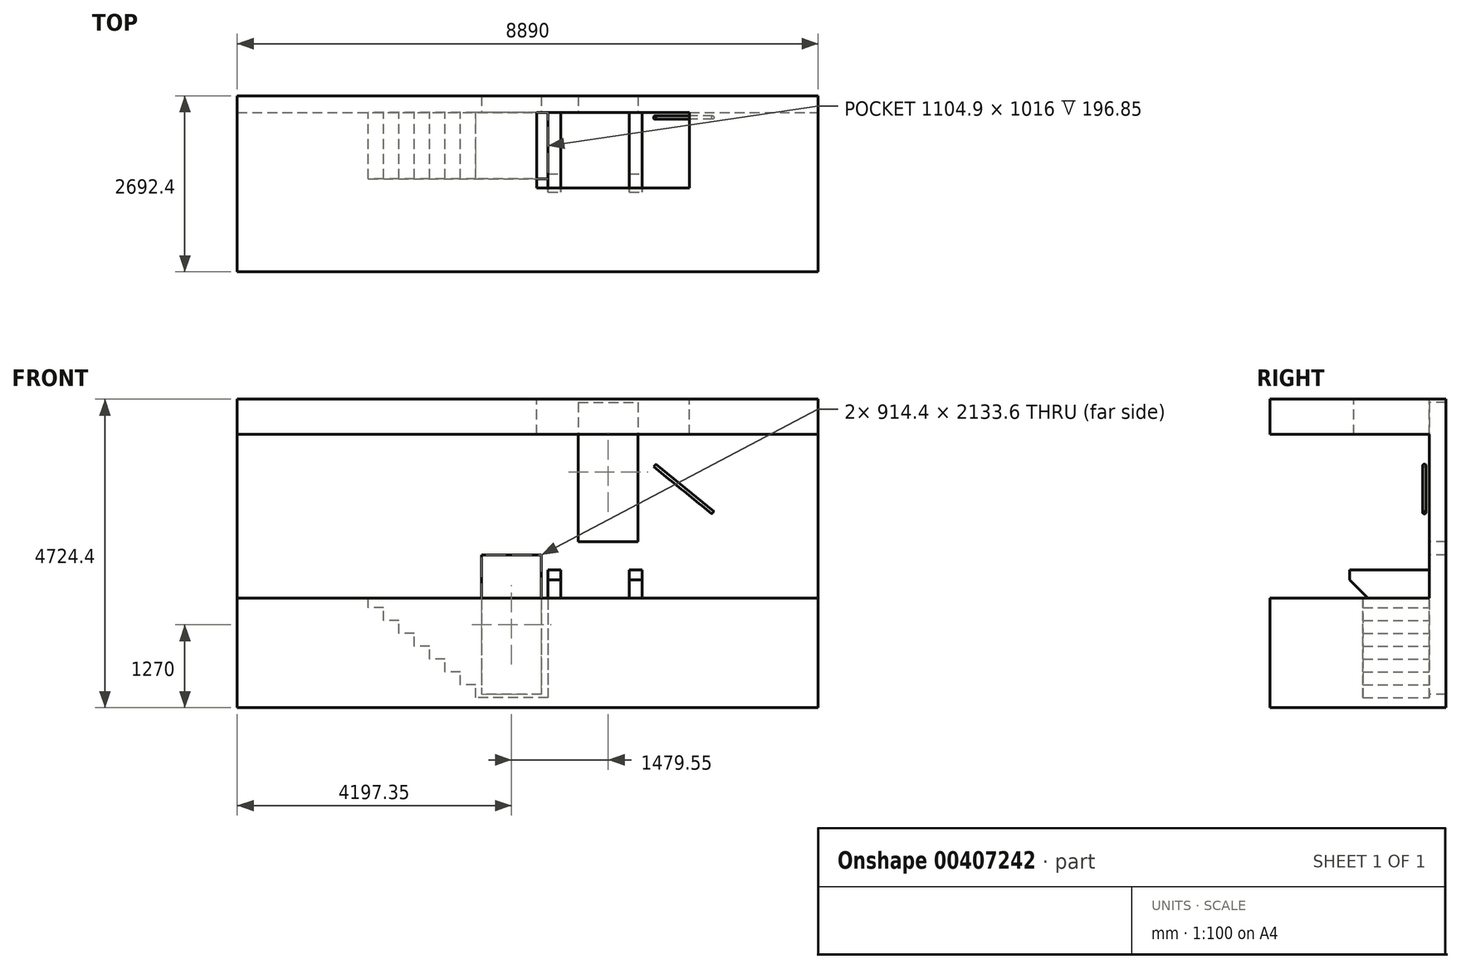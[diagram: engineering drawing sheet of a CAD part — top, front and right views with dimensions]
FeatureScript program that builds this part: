
annotation { "Feature Type Name" : "Feature", "Feature Type Description" : "" }
export const myFeature = defineFeature(function(context is Context, id is Id, definition is map)
    precondition{}
    {
        {
            var Q0;
            Q0=qCreatedBy(makeId("Top.planeOp"),FACE);
            var sketch = newSketch(context, id + "F0", { "sketchPlane" : qUnion([Q0])});
            skLineSegment(sketch, "E0.bottom", {"start": v(-6134.1, 0) * mm, "end": v(2755.9, 0) * mm});
            skLineSegment(sketch, "E0.top", {"start": v(-6134.1, -2438.4) * mm, "end": v(2755.9, -2438.4) * mm});
            skLineSegment(sketch, "E0.left", {"start": v(-6134.1, 0) * mm, "end": v(-6134.1, -2438.4) * mm});
            skLineSegment(sketch, "E0.right", {"start": v(2755.9, 0) * mm, "end": v(2755.9, -2438.4) * mm});
            skSolve(sketch);
        }
        {
            var Q0;
            Q0 = qSketchRegion(id + "F0", true);
            extrude(context, id + "F1", {"entities" : qUnion([Q0]), "oppositeDirection" : true, "depth" : 1676.4 * mm});
        }
        {
            var Q0;
            Q0=makeQuery(id+"F1.opExtrude","SWEPT_FACE",FACE,{"disambiguationData":[OSD([sQuery(id+"F0.wireOp",EDGE,"E0.bottom")])]});
            var sketch = newSketch(context, id + "F2", { "sketchPlane" : qUnion([Q0])});
            skLineSegment(sketch, "E1.top", {"start": v(6134.1, 3048) * mm, "end": v(-2755.9, 3048) * mm});
            skLineSegment(sketch, "E1.left", {"start": v(6134.1, 0) * mm, "end": v(6134.1, 3048) * mm});
            skLineSegment(sketch, "E1.right", {"start": v(-2755.9, 0) * mm, "end": v(-2755.9, 3048) * mm});
            skLineSegment(sketch, "E2.bottom", {"start": v(914.4, 2997.2) * mm, "end": v(0, 2997.2) * mm});
            skLineSegment(sketch, "E2.top", {"start": v(914.4, 863.6) * mm, "end": v(0, 863.6) * mm});
            skLineSegment(sketch, "E2.left", {"start": v(914.4, 2997.2) * mm, "end": v(914.4, 863.6) * mm});
            skLineSegment(sketch, "E2.right", {"start": v(0, 2997.2) * mm, "end": v(0, 863.6) * mm});
            skLineSegment(sketch, "E3.0", {"start": v(6134.1, -1676.4) * mm, "end": v(-2755.9, -1676.4) * mm});
            skLineSegment(sketch, "E4.0", {"start": v(6134.1, -1676.4) * mm, "end": v(6134.1, 0) * mm});
            skLineSegment(sketch, "E5.0", {"start": v(-2755.9, -1676.4) * mm, "end": v(-2755.9, 0) * mm});
            skSolve(sketch);
        }
        {
            var Q0;
            Q0 = qSketchRegion(id + "F2", true);
            extrude(context, id + "F3", {"entities" : qUnion([Q0]), "operationType" : NewBodyOperationType.ADD, "depth" : 254 * mm});
        }
        {
            var Q0;
            Q0=makeQuery(id+"F3.boolean.opBoolean","MERGE",FACE,{"derivedFrom":[makeQuery(id+"F1.opExtrude","SWEPT_FACE",FACE,{"disambiguationData":[OSD([sQuery(id+"F0.wireOp",EDGE,"E0.right")])]}),makeQuery(id+"F3.opExtrude","SWEPT_FACE",FACE,{"disambiguationData":[OSD([sQuery(id+"F2.wireOp",EDGE,"E1.right"),sQuery(id+"F2.wireOp",EDGE,"E5.0")])]})]});
            cPlane(context, id + "F4", {"entities" : qUnion([Q0]), "cplaneType" : CPlaneType.OFFSET, "offset" : 2692.4 * mm, "oppositeDirection" : true, "width" : 152.4 * mm, "height" : 152.4 * mm});
        }
        {
            var Q0;
            Q0=qCreatedBy(id+"F4.planeOp",FACE);
            cPlane(context, id + "F5", {"entities" : qUnion([Q0]), "cplaneType" : CPlaneType.OFFSET, "offset" : 1441.45 * mm, "oppositeDirection" : true, "width" : 152.4 * mm, "height" : 152.4 * mm});
        }
        {
            var Q0;
            Q0=qCreatedBy(id+"F4.planeOp",FACE);
            var sketch = newSketch(context, id + "F6", { "sketchPlane" : qUnion([Q0])});
            skLineSegment(sketch, "E6.0", {"start": v(0, 0) * mm, "end": v(-939.8, 0) * mm});
            skLineSegment(sketch, "E7.0", {"start": v(0, 0) * mm, "end": v(0, 431.8) * mm});
            skLineSegment(sketch, "E8", {"start": v(0, 431.8) * mm, "end": v(-1219.2, 431.8) * mm});
            skLineSegment(sketch, "E9", {"start": v(-1219.2, 431.8) * mm, "end": v(-1219.2, 279.4) * mm});
            skLineSegment(sketch, "E10", {"start": v(-1219.2, 279.4) * mm, "end": v(-939.8, 0) * mm});
            skPoint(sketch, "E11.orphan", {"position": v(-2438.4, 0) * mm});
            skPoint(sketch, "E12.orphan", {"position": v(0, 3048) * mm});
            skSolve(sketch);
        }
        {
            var Q0;
            Q0=makeQuery(id+"F6.imprint","IMPRINT",FACE,{"disambiguationData":[TD([[makeQuery(id+"F6.imprint","IMPRINT",EDGE,{"derivedFrom":sQuery(id+"F6.wireOp",EDGE,"E6.0")}),-1.0]])]});
            var Q1;
            Q1=qCreatedBy(id+"F5.planeOp",FACE);
            extrude(context, id + "F7", {"entities" : qUnion([Q0]), "operationType" : NewBodyOperationType.ADD, "endBound" : BoundingType.UP_TO_SURFACE, "oppositeDirection" : true, "endBoundEntityFace" : qUnion([Q1]), "depth" : 196.85 * mm});
        }
        {
            var Q0;
            Q0=makeQuery(id+"F7.opExtrude","SWEPT_FACE",FACE,{"disambiguationData":[OSD([sQuery(id+"F6.wireOp",EDGE,"E8")])]});
            var sketch = newSketch(context, id + "F8", { "sketchPlane" : qUnion([Q0])});
            skLineSegment(sketch, "E13.bottom", {"start": v(-1181.1, 0) * mm, "end": v(-133.35, 0) * mm});
            skLineSegment(sketch, "E13.top", {"start": v(-1181.1, -1219.2) * mm, "end": v(-133.35, -1219.2) * mm});
            skLineSegment(sketch, "E13.left", {"start": v(-1181.1, 0) * mm, "end": v(-1181.1, -1219.2) * mm});
            skLineSegment(sketch, "E13.right", {"start": v(-133.35, 0) * mm, "end": v(-133.35, -1219.2) * mm});
            skSolve(sketch);
        }
        {
            var Q0;
            Q0=makeQuery(id+"F8.imprint","IMPRINT",FACE,{"disambiguationData":[TD([[makeQuery(id+"F8.imprint","IMPRINT",EDGE,{"derivedFrom":sQuery(id+"F8.wireOp",EDGE,"E13.bottom")}),-1.0]])]});
            var Q1;
            Q1=makeQuery(id+"F1.opExtrude","CAP_FACE",FACE,{"disambiguationData":[OSD([sQuery(id+"F0.wireOp",EDGE,"E0.bottom"),sQuery(id+"F0.wireOp",EDGE,"E0.top"),sQuery(id+"F0.wireOp",EDGE,"E0.left"),sQuery(id+"F0.wireOp",EDGE,"E0.right")])],"isStart":true});
            extrude(context, id + "F9", {"entities" : qUnion([Q0]), "operationType" : NewBodyOperationType.REMOVE, "endBound" : BoundingType.UP_TO_SURFACE, "oppositeDirection" : true, "endBoundEntityFace" : qUnion([Q1]), "depth" : 25.4 * mm});
        }
        {
            var Q0;
            Q0=makeQuery(id+"F9.boolean.opBoolean","MERGE",FACE,{"derivedFrom":[makeQuery(id+"F3.opExtrude","CAP_FACE",FACE,{"disambiguationData":[OSD([sQuery(id+"F2.wireOp",EDGE,"E1.top"),sQuery(id+"F2.wireOp",EDGE,"E1.left"),sQuery(id+"F2.wireOp",EDGE,"E1.right"),sQuery(id+"F2.wireOp",EDGE,"E2.bottom"),sQuery(id+"F2.wireOp",EDGE,"E2.top"),sQuery(id+"F2.wireOp",EDGE,"E2.left"),sQuery(id+"F2.wireOp",EDGE,"E2.right"),sQuery(id+"F2.wireOp",EDGE,"E3.0"),sQuery(id+"F2.wireOp",EDGE,"E4.0"),sQuery(id+"F2.wireOp",EDGE,"E5.0")])],"isStart":true}),makeQuery(id+"F9.opExtrude","SWEPT_FACE",FACE,{"disambiguationData":[OSD([sQuery(id+"F8.wireOp",EDGE,"E13.bottom")])]})]});
            var sketch = newSketch(context, id + "F10", { "sketchPlane" : qUnion([Q0])});
            skLineSegment(sketch, "E14", {"start": v(-1377.95, 0) * mm, "end": v(-1377.95, -1524) * mm});
            skLineSegment(sketch, "E15", {"start": v(-1377.95, -1524) * mm, "end": v(-2482.85, -1524) * mm});
            skLineSegment(sketch, "E16", {"start": v(-2482.85, -1524) * mm, "end": v(-2482.85, -1327.15) * mm});
            skLineSegment(sketch, "E17", {"start": v(-2482.85, -1327.15) * mm, "end": v(-2717.8, -1327.15) * mm});
            skLineSegment(sketch, "E18", {"start": v(-2717.8, -1327.15) * mm, "end": v(-2717.8, -1130.3) * mm});
            skLineSegment(sketch, "E19", {"start": v(-2717.8, -1130.3) * mm, "end": v(-2952.75, -1130.3) * mm});
            skLineSegment(sketch, "E20", {"start": v(-2952.75, -1130.3) * mm, "end": v(-2952.75, -933.45) * mm});
            skLineSegment(sketch, "E21", {"start": v(-2952.75, -933.45) * mm, "end": v(-3187.7, -933.45) * mm});
            skLineSegment(sketch, "E22", {"start": v(-3187.7, -933.45) * mm, "end": v(-3187.7, -736.6) * mm});
            skLineSegment(sketch, "E23", {"start": v(-3187.7, -736.6) * mm, "end": v(-3422.65, -736.6) * mm});
            skLineSegment(sketch, "E24", {"start": v(-3422.65, -736.6) * mm, "end": v(-3422.65, -539.75) * mm});
            skLineSegment(sketch, "E25", {"start": v(-3422.65, -539.75) * mm, "end": v(-3657.6, -539.75) * mm});
            skLineSegment(sketch, "E26", {"start": v(-3657.6, -539.75) * mm, "end": v(-3657.6, -342.9) * mm});
            skLineSegment(sketch, "E27", {"start": v(-3657.6, -342.9) * mm, "end": v(-3892.55, -342.9) * mm});
            skLineSegment(sketch, "E28", {"start": v(-3892.55, -342.9) * mm, "end": v(-3892.55, -146.05) * mm});
            skLineSegment(sketch, "E29", {"start": v(-1377.95, 0) * mm, "end": v(-4127.5, 0) * mm});
            skLineSegment(sketch, "E30", {"start": v(-3892.55, -146.05) * mm, "end": v(-4127.5, -146.05) * mm});
            skLineSegment(sketch, "E31", {"start": v(-4127.5, -146.05) * mm, "end": v(-4127.5, 0) * mm});
            skSolve(sketch);
        }
        {
            var Q0;
            Q0 = qSketchRegion(id + "F10", true);
            extrude(context, id + "F11", {"entities" : qUnion([Q0]), "operationType" : NewBodyOperationType.REMOVE, "depth" : 1016 * mm});
        }
        {
            var Q0;
            Q0=makeQuery(id+"F3.opExtrude","SWEPT_FACE",FACE,{"disambiguationData":[OSD([sQuery(id+"F2.wireOp",EDGE,"E1.top")])]});
            var sketch = newSketch(context, id + "F12", { "sketchPlane" : qUnion([Q0])});
            skLineSegment(sketch, "E32.0", {"start": v(-6134.1, 0) * mm, "end": v(-6134.1, -2438.4) * mm});
            skLineSegment(sketch, "E33.0", {"start": v(-6134.1, -2438.4) * mm, "end": v(2755.9, -2438.4) * mm});
            skLineSegment(sketch, "E34.0", {"start": v(2755.9, 0) * mm, "end": v(2755.9, -2438.4) * mm});
            skLineSegment(sketch, "E35.0", {"start": v(-6134.1, 0) * mm, "end": v(-1549.4, 0) * mm});
            skLineSegment(sketch, "E36", {"start": v(-1549.4, 0) * mm, "end": v(-1549.4, -1155.7) * mm});
            skLineSegment(sketch, "E37", {"start": v(-1549.4, -1155.7) * mm, "end": v(787.4, -1155.7) * mm});
            skLineSegment(sketch, "E38", {"start": v(787.4, -1155.7) * mm, "end": v(787.4, 0) * mm});
            skLineSegment(sketch, "E39.trimOffspring", {"start": v(787.4, 0) * mm, "end": v(2755.9, 0) * mm});
            skSolve(sketch);
        }
        {
            var Q0;
            Q0 = qSketchRegion(id + "F12", true);
            extrude(context, id + "F13", {"entities" : qUnion([Q0]), "operationType" : NewBodyOperationType.ADD, "oppositeDirection" : true, "depth" : 539.75 * mm});
        }
        {
            var Q0;
            Q0=makeQuery(id+"F11.boolean.opBoolean","MERGE",FACE,{"derivedFrom":[makeQuery(id+"F9.boolean.opBoolean","MERGE",FACE,{"derivedFrom":[makeQuery(id+"F3.opExtrude","CAP_FACE",FACE,{"disambiguationData":[OSD([sQuery(id+"F2.wireOp",EDGE,"E1.top"),sQuery(id+"F2.wireOp",EDGE,"E1.left"),sQuery(id+"F2.wireOp",EDGE,"E1.right"),sQuery(id+"F2.wireOp",EDGE,"E2.bottom"),sQuery(id+"F2.wireOp",EDGE,"E2.top"),sQuery(id+"F2.wireOp",EDGE,"E2.left"),sQuery(id+"F2.wireOp",EDGE,"E2.right"),sQuery(id+"F2.wireOp",EDGE,"E3.0"),sQuery(id+"F2.wireOp",EDGE,"E4.0"),sQuery(id+"F2.wireOp",EDGE,"E5.0")])],"isStart":true}),makeQuery(id+"F9.opExtrude","SWEPT_FACE",FACE,{"disambiguationData":[OSD([sQuery(id+"F8.wireOp",EDGE,"E13.bottom")])]})]}),makeQuery(id+"F11.opExtrude","CAP_FACE",FACE,{"disambiguationData":[OSD([sQuery(id+"F10.wireOp",EDGE,"E14"),sQuery(id+"F10.wireOp",EDGE,"E15"),sQuery(id+"F10.wireOp",EDGE,"E16"),sQuery(id+"F10.wireOp",EDGE,"E17"),sQuery(id+"F10.wireOp",EDGE,"E18"),sQuery(id+"F10.wireOp",EDGE,"E19"),sQuery(id+"F10.wireOp",EDGE,"E20"),sQuery(id+"F10.wireOp",EDGE,"E21"),sQuery(id+"F10.wireOp",EDGE,"E22"),sQuery(id+"F10.wireOp",EDGE,"E23"),sQuery(id+"F10.wireOp",EDGE,"E24"),sQuery(id+"F10.wireOp",EDGE,"E25"),sQuery(id+"F10.wireOp",EDGE,"E26"),sQuery(id+"F10.wireOp",EDGE,"E27"),sQuery(id+"F10.wireOp",EDGE,"E28"),sQuery(id+"F10.wireOp",EDGE,"E29"),sQuery(id+"F10.wireOp",EDGE,"E30"),sQuery(id+"F10.wireOp",EDGE,"E31")])],"isStart":true})]});
            cPlane(context, id + "F14", {"entities" : qUnion([Q0]), "cplaneType" : CPlaneType.OFFSET, "offset" : 76.2 * mm, "width" : 152.4 * mm, "height" : 152.4 * mm});
        }
        {
            var Q0;
            Q0=qCreatedBy(id+"F14.planeOp",FACE);
            var sketch = newSketch(context, id + "F15", { "sketchPlane" : qUnion([Q0])});
            skLineSegment(sketch, "E40", {"start": v(254, 2032) * mm, "end": v(1143, 1311.33) * mm});
            skPoint(sketch, "E41", {"position": v(1143, 1311.33) * mm});
            skPoint(sketch, "E42", {"position": v(254, 2032) * mm});
            skSolve(sketch);
        }
        {
            var Q0;
            Q0=sQuery(id+"F15.wireOp",VERTEX,"E41");
            var Q1;
            Q1=sQuery(id+"F15.wireOp",EDGE,"E40");
            cPlane(context, id + "F16", {"entities" : qUnion([Q0, Q1]), "cplaneType" : CPlaneType.LINE_POINT, "offset" : 25.4 * mm, "width" : 152.4 * mm, "height" : 152.4 * mm});
        }
        {
            var Q0;
            Q0=qCreatedBy(id+"F16.planeOp",FACE);
            var sketch = newSketch(context, id + "F17", { "sketchPlane" : qUnion([Q0])});
            skCircle(sketch, "E43", {"center": v(-76.2, 1738.44) * mm, "radius": 25.4 * mm});
            skSolve(sketch);
        }
        {
            var Q0;
            Q0=makeQuery(id+"F17.imprint","IMPRINT",FACE,{"disambiguationData":[TD([[makeQuery(id+"F17.imprint","IMPRINT",EDGE,{"derivedFrom":sQuery(id+"F17.wireOp",EDGE,"E43")}),1.0]])]});
            var Q1;
            Q1=sQuery(id+"F15.wireOp",EDGE,"E40");
            sweep(context, id + "F18", {"profiles" : qUnion([Q0]), "path" : qUnion([Q1])});
        }
        {
            var Q0;
            Q0=makeQuery(id+"F11.boolean.opBoolean","MERGE",FACE,{"derivedFrom":[makeQuery(id+"F9.boolean.opBoolean","MERGE",FACE,{"derivedFrom":[makeQuery(id+"F3.opExtrude","CAP_FACE",FACE,{"disambiguationData":[OSD([sQuery(id+"F2.wireOp",EDGE,"E1.top"),sQuery(id+"F2.wireOp",EDGE,"E1.left"),sQuery(id+"F2.wireOp",EDGE,"E1.right"),sQuery(id+"F2.wireOp",EDGE,"E2.bottom"),sQuery(id+"F2.wireOp",EDGE,"E2.top"),sQuery(id+"F2.wireOp",EDGE,"E2.left"),sQuery(id+"F2.wireOp",EDGE,"E2.right"),sQuery(id+"F2.wireOp",EDGE,"E3.0"),sQuery(id+"F2.wireOp",EDGE,"E4.0"),sQuery(id+"F2.wireOp",EDGE,"E5.0")])],"isStart":true}),makeQuery(id+"F9.opExtrude","SWEPT_FACE",FACE,{"disambiguationData":[OSD([sQuery(id+"F8.wireOp",EDGE,"E13.bottom")])]})]}),makeQuery(id+"F11.opExtrude","CAP_FACE",FACE,{"disambiguationData":[OSD([sQuery(id+"F10.wireOp",EDGE,"E14"),sQuery(id+"F10.wireOp",EDGE,"E15"),sQuery(id+"F10.wireOp",EDGE,"E16"),sQuery(id+"F10.wireOp",EDGE,"E17"),sQuery(id+"F10.wireOp",EDGE,"E18"),sQuery(id+"F10.wireOp",EDGE,"E19"),sQuery(id+"F10.wireOp",EDGE,"E20"),sQuery(id+"F10.wireOp",EDGE,"E21"),sQuery(id+"F10.wireOp",EDGE,"E22"),sQuery(id+"F10.wireOp",EDGE,"E23"),sQuery(id+"F10.wireOp",EDGE,"E24"),sQuery(id+"F10.wireOp",EDGE,"E25"),sQuery(id+"F10.wireOp",EDGE,"E26"),sQuery(id+"F10.wireOp",EDGE,"E27"),sQuery(id+"F10.wireOp",EDGE,"E28"),sQuery(id+"F10.wireOp",EDGE,"E29"),sQuery(id+"F10.wireOp",EDGE,"E30"),sQuery(id+"F10.wireOp",EDGE,"E31")])],"isStart":true})]});
            var sketch = newSketch(context, id + "F19", { "sketchPlane" : qUnion([Q0])});
            skLineSegment(sketch, "E44.bottom", {"start": v(-1479.55, 660.4) * mm, "end": v(-2393.95, 660.4) * mm});
            skLineSegment(sketch, "E44.top", {"start": v(-1479.55, -1473.2) * mm, "end": v(-2393.95, -1473.2) * mm});
            skLineSegment(sketch, "E44.left", {"start": v(-1479.55, 660.4) * mm, "end": v(-1479.55, -1473.2) * mm});
            skLineSegment(sketch, "E44.right", {"start": v(-2393.95, 660.4) * mm, "end": v(-2393.95, -1473.2) * mm});
            skSolve(sketch);
        }
        {
            var Q0;
            Q0=makeQuery(id+"F19.imprint","IMPRINT",FACE,{"disambiguationData":[TD([[makeQuery(id+"F19.imprint","IMPRINT",EDGE,{"derivedFrom":sQuery(id+"F19.wireOp",EDGE,"E44.bottom")}),1.0]])]});
            var Q1;
            Q1=makeQuery(id+"F3.opExtrude","CAP_FACE",FACE,{"disambiguationData":[OSD([sQuery(id+"F2.wireOp",EDGE,"E1.top"),sQuery(id+"F2.wireOp",EDGE,"E1.left"),sQuery(id+"F2.wireOp",EDGE,"E1.right"),sQuery(id+"F2.wireOp",EDGE,"E2.bottom"),sQuery(id+"F2.wireOp",EDGE,"E2.top"),sQuery(id+"F2.wireOp",EDGE,"E2.left"),sQuery(id+"F2.wireOp",EDGE,"E2.right"),sQuery(id+"F2.wireOp",EDGE,"E3.0"),sQuery(id+"F2.wireOp",EDGE,"E4.0"),sQuery(id+"F2.wireOp",EDGE,"E5.0")])],"isStart":false});
            extrude(context, id + "F20", {"entities" : qUnion([Q0]), "operationType" : NewBodyOperationType.REMOVE, "endBound" : BoundingType.UP_TO_SURFACE, "oppositeDirection" : true, "endBoundEntityFace" : qUnion([Q1]), "depth" : 25.4 * mm});
        }
    });
